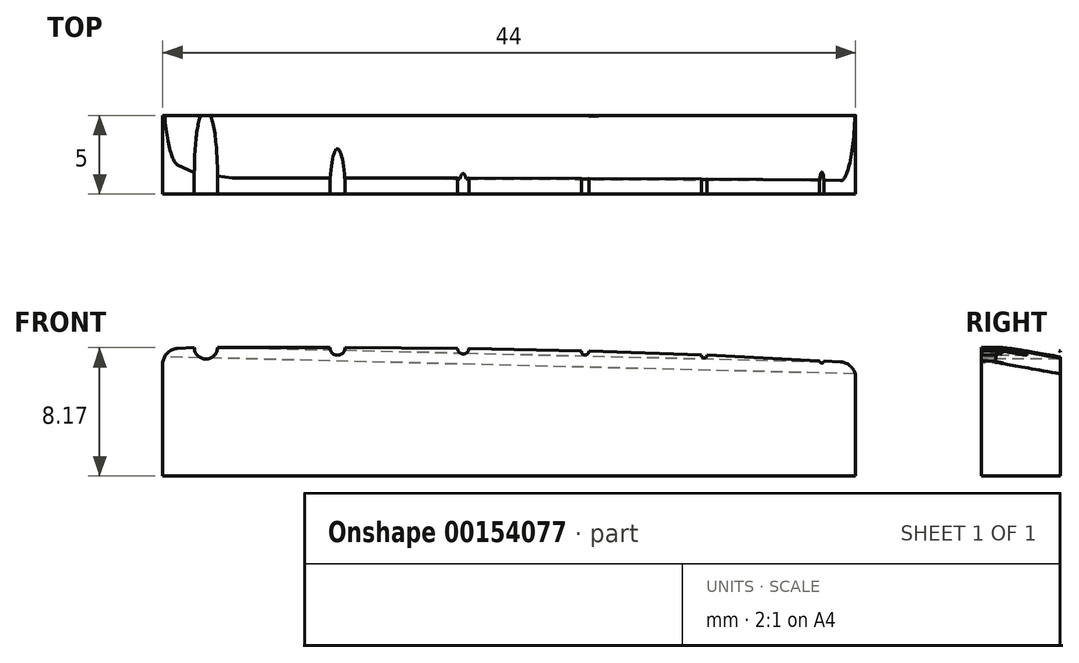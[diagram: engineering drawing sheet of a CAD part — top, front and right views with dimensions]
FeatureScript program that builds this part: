
annotation { "Feature Type Name" : "Feature", "Feature Type Description" : "" }
export const myFeature = defineFeature(function(context is Context, id is Id, definition is map)
    precondition{}
    {
        {
            var Q0;
            Q0=qCreatedBy(makeId("Front.planeOp"),FACE);
            var sketch = newSketch(context, id + "F0", { "sketchPlane" : qUnion([Q0])});
            skLineSegment(sketch, "E0", {"start": v(0, 0) * mm, "end": v(22, 0) * mm});
            skLineSegment(sketch, "E1", {"start": v(22, 0) * mm, "end": v(22, 9) * mm});
            skLineSegment(sketch, "E2", {"start": v(0, 0) * mm, "end": v(-22, 0) * mm});
            skLineSegment(sketch, "E3", {"start": v(-22, 0) * mm, "end": v(-22, 9) * mm});
            skPoint(sketch, "E4", {"position": v(22, 7.07) * mm});
            skPoint(sketch, "E5", {"position": v(-22, 7.32) * mm});
            skArc(sketch, "E6", {"start": v(22, 7.07) * mm, "mid": v(0, 7.76) * mm, "end": v(-22, 7.32) * mm, "construction": true});
            skArc(sketch, "E7", {"start": v(-20, 8.17) * mm, "mid": v(-19.26, 7.44) * mm, "end": v(-18.52, 8.17) * mm});
            skArc(sketch, "E8", {"start": v(-11.38, 8.16) * mm, "mid": v(-10.9, 7.68) * mm, "end": v(-10.42, 8.16) * mm});
            skArc(sketch, "E9", {"start": v(-3.28, 8.12) * mm, "mid": v(-2.92, 7.76) * mm, "end": v(-2.56, 8.12) * mm});
            skArc(sketch, "E10", {"start": v(4.58, 7.94) * mm, "mid": v(4.82, 7.7) * mm, "end": v(5.06, 7.94) * mm});
            skArc(sketch, "E11", {"start": v(12.2, 7.7) * mm, "mid": v(12.4, 7.5) * mm, "end": v(12.58, 7.7) * mm});
            skArc(sketch, "E12", {"start": v(19.72, 7.32) * mm, "mid": v(19.86, 7.18) * mm, "end": v(20, 7.32) * mm});
            skLineSegment(sketch, "E13", {"start": v(-20, 8.17) * mm, "end": v(-22, 8.06) * mm});
            skLineSegment(sketch, "E14", {"start": v(-18.52, 8.17) * mm, "end": v(-11.38, 8.16) * mm});
            skLineSegment(sketch, "E15", {"start": v(-10.42, 8.16) * mm, "end": v(-3.28, 8.12) * mm});
            skLineSegment(sketch, "E16", {"start": v(-2.56, 8.12) * mm, "end": v(4.58, 7.94) * mm});
            skLineSegment(sketch, "E17", {"start": v(5.06, 7.94) * mm, "end": v(12.2, 7.7) * mm});
            skLineSegment(sketch, "E18", {"start": v(12.58, 7.7) * mm, "end": v(19.72, 7.32) * mm});
            skLineSegment(sketch, "E19", {"start": v(20, 7.32) * mm, "end": v(22, 7.2) * mm});
            skSolve(sketch);
        }
        {
            var Q0;
            Q0 = qSketchRegion(id + "F0", true);
            extrude(context, id + "F1", {"entities" : qUnion([Q0]), "oppositeDirection" : true, "depth" : 5 * mm});
        }
        {
            var Q0;
            Q0=makeQuery(id+"F1.opExtrude","SWEPT_EDGE",EDGE,{"disambiguationData":[OSD([sQuery(id+"F0.wireOp",EDGE,"E1"),sQuery(id+"F0.wireOp",EDGE,"E19")])]});
            var Q1;
            Q1=makeQuery(id+"F1.opExtrude","SWEPT_EDGE",EDGE,{"disambiguationData":[OSD([sQuery(id+"F0.wireOp",EDGE,"E3"),sQuery(id+"F0.wireOp",EDGE,"E13")])]});
            fillet(context, id + "F2", {"entities" : qUnion([Q0, Q1]), "radius" : 1 * mm, "tangentPropagation" : true, "allowEdgeOverflow" : false});
        }
        {
            var Q0;
            Q0=makeQuery(id+"F1.opExtrude","CAP_EDGE",EDGE,{"disambiguationData":[OSD([sQuery(id+"F0.wireOp",EDGE,"E16")])],"isStart":false});
            cPlane(context, id + "F3", {"entities" : qUnion([Q0]), "cplaneType" : CPlaneType.LINE_ANGLE, "offset" : 25 * mm, "angle" : 80 * degree, "width" : 150 * mm, "height" : 150 * mm});
        }
        {
            var Q0;
            Q0=qCreatedBy(id+"F3.planeOp",FACE);
            var sketch = newSketch(context, id + "F4", { "sketchPlane" : qUnion([Q0])});
            skPoint(sketch, "E20.0", {"position": v(-21.25, -1.4) * mm});
            skLineSegment(sketch, "E21", {"start": v(-26.86, -0.4) * mm, "end": v(37.28, -0.4) * mm});
            skLineSegment(sketch, "E22", {"start": v(37.28, -0.4) * mm, "end": v(37.28, 7.6) * mm});
            skLineSegment(sketch, "E23", {"start": v(37.28, 7.6) * mm, "end": v(-26.86, 7.6) * mm});
            skLineSegment(sketch, "E24", {"start": v(-26.86, 7.6) * mm, "end": v(-26.86, -0.4) * mm});
            skSolve(sketch);
        }
        {
            var Q0;
            Q0 = qSketchRegion(id + "F4", true);
            extrude(context, id + "F5", {"entities" : qUnion([Q0]), "operationType" : NewBodyOperationType.REMOVE, "oppositeDirection" : true, "depth" : 1 * mm});
        }
    });
